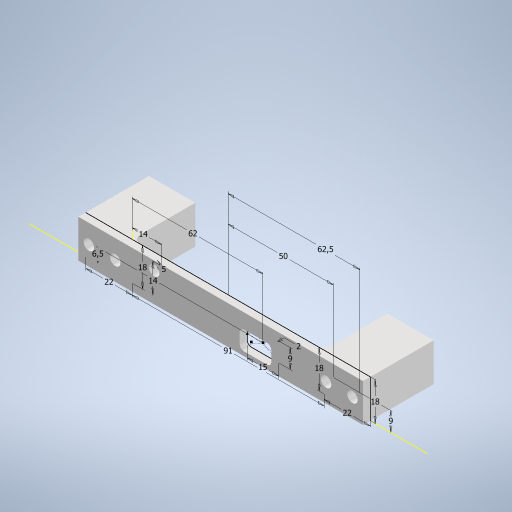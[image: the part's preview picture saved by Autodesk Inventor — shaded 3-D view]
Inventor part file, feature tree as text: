
AUTODESK INVENTOR PART (.ipt)
format: ipt  version: 2024.3 (Build 283343000, 343)  size: 281,088 bytes
history: native  units: in
note: dims shown in document units (in); Inventor stores cm internally (conversion verified against a paired STEP export)
features: extrude x2, sketch x1, hole x1, fillet x1
ambient origin geometry x8: Origin, YZ Plane, XZ Plane, XY Plane, X Axis, Y Axis, Z Axis, Center Point
bodies: Body1 (feature_tree)
feature tree (5):
  sketch  "Sketch3"  dims[d26=0.1969in d29=0.5906in d30=0.3543in d31=0.0787in d34=3.5827in d35=0.7087in d36=0.8661in d37=0.7087in d38=0.8661in d39=0.7087in d41=0.5512in d42=0.5512in d44=0.1378in d45=0.0in d46=1.1811in d47=0.0in d48=0.1969in d49=0.2362in d50=0.1575in d51=0.0787in d52=90.0deg d53=0.315in d54=0.8108in d55=0.1575in d56=2.4409in d57=0.2559in d60=1.9685in d61=2.4606in d62=0.3543in]
  extrude  "Extrusion4"  Depth=3.5827in
  extrude  "Extrusion5"  Depth=0.7087in
  hole  "Hole1"  [1 undecoded]
  fillet  "Fillet1"  Radius=0.7087in
note: 1 required parameter value undecoded (feature->parameter linkage not recoverable at this tier; creation-order binding heuristic only, values carry confidence <= 0.55)
